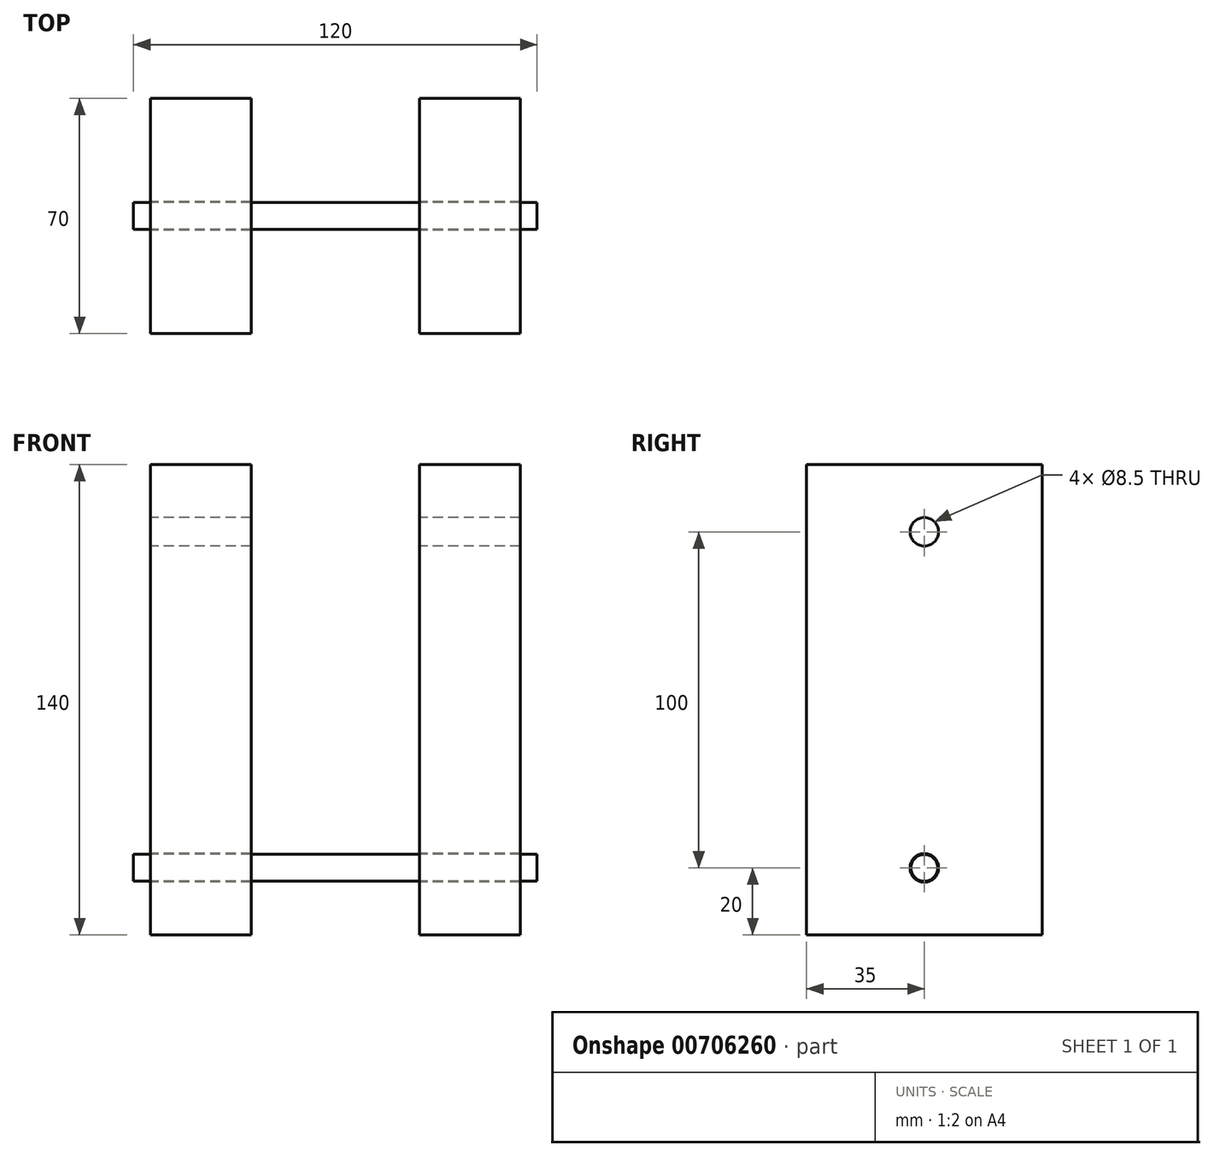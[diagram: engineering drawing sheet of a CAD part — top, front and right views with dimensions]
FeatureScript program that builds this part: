
annotation { "Feature Type Name" : "Feature", "Feature Type Description" : "" }
export const myFeature = defineFeature(function(context is Context, id is Id, definition is map)
    precondition{}
    {
        {
            var Q0;
            Q0=qCreatedBy(makeId("Right.planeOp"),FACE);
            var sketch = newSketch(context, id + "F0", { "sketchPlane" : qUnion([Q0])});
            skLineSegment(sketch, "E0", {"start": v(0, 0) * mm, "end": v(0, -120) * mm});
            skLineSegment(sketch, "E1.bottom", {"start": v(35, -130) * mm, "end": v(-35, -130) * mm});
            skLineSegment(sketch, "E1.top", {"start": v(35, 10) * mm, "end": v(-35, 10) * mm});
            skLineSegment(sketch, "E1.left", {"start": v(35, -130) * mm, "end": v(35, 10) * mm});
            skLineSegment(sketch, "E1.right", {"start": v(-35, -130) * mm, "end": v(-35, 10) * mm});
            skPoint(sketch, "E1.middle", {"position": v(0, -60) * mm});
            skLineSegment(sketch, "E2", {"start": v(-24.21, -130) * mm, "end": v(-24.21, -110) * mm});
            skLineSegment(sketch, "E3", {"start": v(-24.21, -110) * mm, "end": v(0, -110) * mm});
            skCircle(sketch, "E4", {"center": v(0, -110) * mm, "radius": 4.25 * mm});
            skLineSegment(sketch, "E5", {"start": v(-10.59, 10) * mm, "end": v(-10.59, -10) * mm});
            skLineSegment(sketch, "E6", {"start": v(-10.59, -10) * mm, "end": v(0, -10) * mm});
            skCircle(sketch, "E7", {"center": v(0, -10) * mm, "radius": 4.25 * mm});
            skSolve(sketch);
        }
        {
            var Q0;
            Q0 = qSketchRegion(id + "F0", true);
            extrude(context, id + "F1", {"entities" : qUnion([Q0]), "depth" : 30 * mm, "offsetDistance" : 25 * mm});
        }
        {
            var Q0;
            Q0=makeQuery(id+"F1.opExtrude","SWEPT_BODY",BODY,{"disambiguationData":[OSD([sQuery(id+"F0.wireOp",EDGE,"E1.bottom"),sQuery(id+"F0.wireOp",EDGE,"E1.top"),sQuery(id+"F0.wireOp",EDGE,"E1.left"),sQuery(id+"F0.wireOp",EDGE,"E1.right"),sQuery(id+"F0.wireOp",EDGE,"E4"),sQuery(id+"F0.wireOp",EDGE,"E7")])]});
            transform(context, id + "F2", {"entities" : qUnion([Q0]), "transformType" : TransformType.TRANSLATION_3D, "dx" : -30 * mm, "dy" : 0 * mm, "dz" : 0 * mm, "makeCopy" : true});
        }
        {
            var Q0;
            Q0=makeQuery(id+"F2.opPattern","COPY",BODY,{"derivedFrom":makeQuery(id+"F1.opExtrude","SWEPT_BODY",BODY,{"disambiguationData":[OSD([sQuery(id+"F0.wireOp",EDGE,"E1.bottom"),sQuery(id+"F0.wireOp",EDGE,"E1.top"),sQuery(id+"F0.wireOp",EDGE,"E1.left"),sQuery(id+"F0.wireOp",EDGE,"E1.right"),sQuery(id+"F0.wireOp",EDGE,"E4"),sQuery(id+"F0.wireOp",EDGE,"E7")])]}),"instanceName":"1"});
            transform(context, id + "F3", {"entities" : qUnion([Q0]), "transformType" : TransformType.TRANSLATION_3D, "dx" : -25 * mm, "dy" : 0 * mm, "dz" : 0 * mm, "makeCopy" : false});
        }
        {
            var Q0;
            Q0=makeQuery(id+"F1.opExtrude","SWEPT_BODY",BODY,{"disambiguationData":[OSD([sQuery(id+"F0.wireOp",EDGE,"E1.bottom"),sQuery(id+"F0.wireOp",EDGE,"E1.top"),sQuery(id+"F0.wireOp",EDGE,"E1.left"),sQuery(id+"F0.wireOp",EDGE,"E1.right"),sQuery(id+"F0.wireOp",EDGE,"E4"),sQuery(id+"F0.wireOp",EDGE,"E7")])]});
            transform(context, id + "F4", {"entities" : qUnion([Q0]), "transformType" : TransformType.TRANSLATION_3D, "dx" : 25 * mm, "dy" : 0 * mm, "dz" : 0 * mm, "makeCopy" : false});
        }
        {
            var Q0;
            Q0=qCreatedBy(makeId("Right.planeOp"),FACE);
            var sketch = newSketch(context, id + "F5", { "sketchPlane" : qUnion([Q0])});
            skLineSegment(sketch, "E8", {"start": v(0, 0) * mm, "end": v(0, -110) * mm});
            skCircle(sketch, "E9", {"center": v(0, -110) * mm, "radius": 4 * mm});
            skSolve(sketch);
        }
        {
            var Q0;
            Q0 = qSketchRegion(id + "F5", true);
            extrude(context, id + "F6", {"entities" : qUnion([Q0]), "endBound" : BoundingType.SYMMETRIC, "depth" : 120 * mm, "offsetDistance" : 25 * mm});
        }
    });
